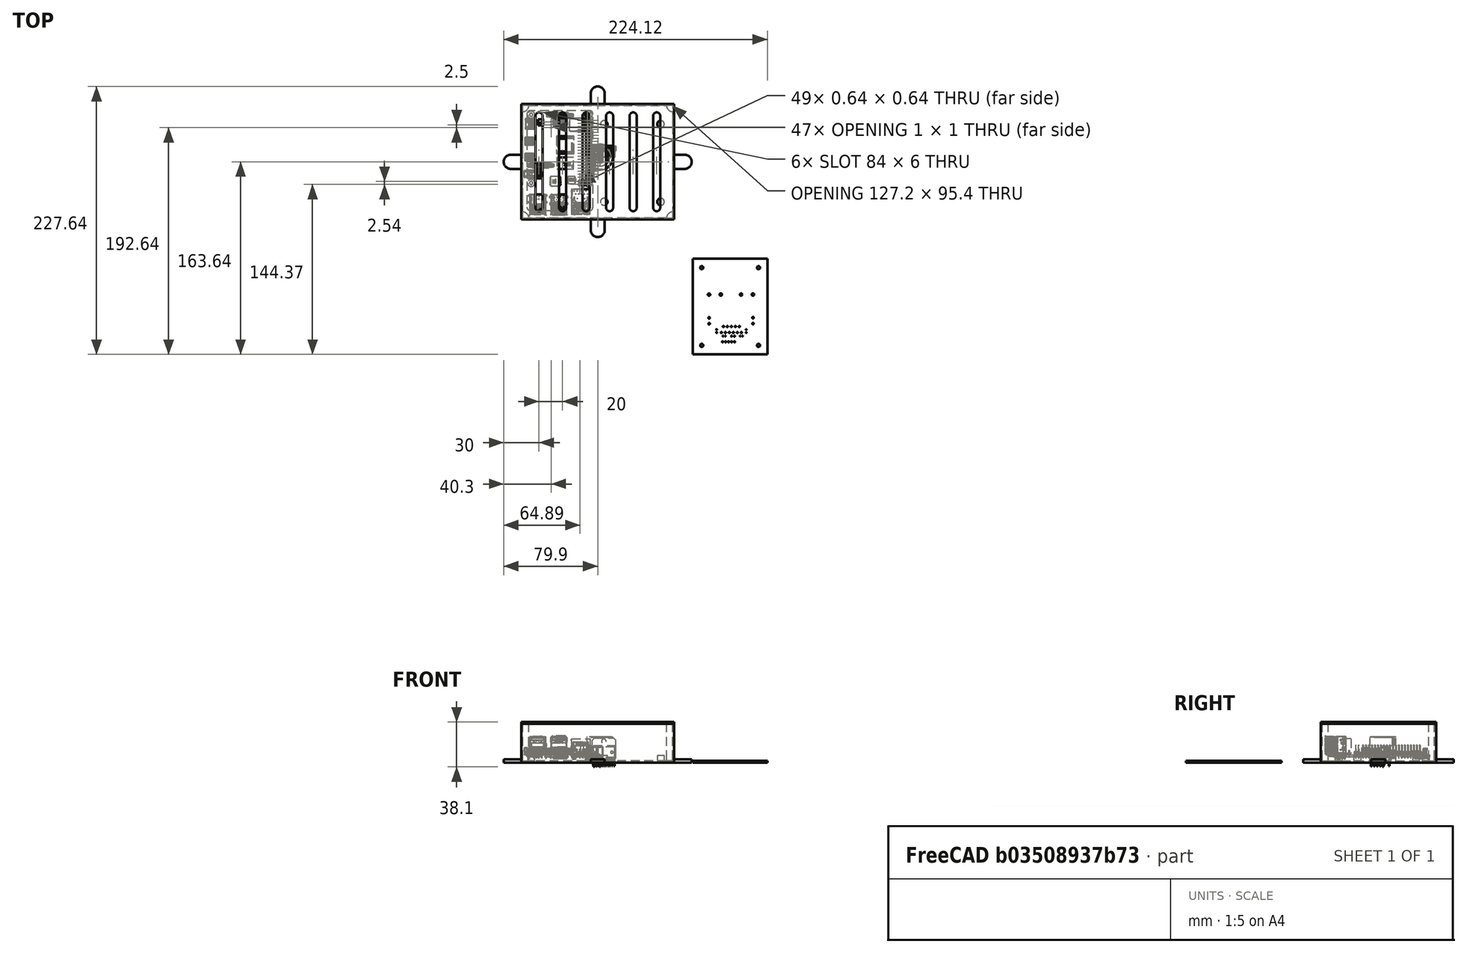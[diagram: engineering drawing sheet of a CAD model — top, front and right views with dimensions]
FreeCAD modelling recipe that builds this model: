
FCSTD DOCUMENT  (FreeCAD 0.19R)
Label: cmd-module-box
License: All rights reserved
LicenseURL: http://en.wikipedia.org/wiki/All_rights_reserved
objects: App::Part×14, Part::Feature×13, Sketcher::SketchObject×12, PartDesign::Pad×12, PartDesign::Body×12, Part::MultiFuse×6, Part::Fuse×4, Mesh::Feature×2
note: 71 computed .brp shape members not serialized (recipe doc carries the construction recipe); baked Part::Feature solids carry a one-line shape summary decoded from their .brp

FEATURE [Part::Feature] Feature  label="Raspberry Pi 4 Model B001"
  Placement = pos=(-29,-3,6) rot=(0.57735,-0.57735,-0.57735;2.0944rad)
  shape: bbox 58.41 x 89 x 19.91 mm, 10487 faces, 109 solids (baked)
FEATURE [Part::Feature] Part__Feature  label="SOLID"
  shape: bbox 2.54 x 12.7 x 11.54 mm, 124 faces (baked)
FEATURE [App::Part] PinHeader_1x05_P2_54mm_Vertical  label="PinHeader_1x05_P2.54mm_Vertical"
  Group = -> [Part__Feature]
  Origin = -> Origin012
  Placement = pos=(109.22,-156.972,1.65) rot=(0,0,1;1.5708rad)
FEATURE [Part::Feature] Part__Feature001  label="SOLID001"
  shape: bbox 10.74 x 9.8 x 17.3 mm, 89 faces (baked)
FEATURE [App::Part] TerminalBlock_Phoenix_MKDS_1_5_2_1x02_P5_00mm_Horizontal  label="TerminalBlock_Phoenix_MKDS-1,5-2_1x02_P5.00mm_Horizontal"
  Group = -> [Part__Feature001]
  Origin = -> Origin013
  Placement = pos=(135.128,-141.478,1.65) rot=(0,0,1;1.5708rad)
FEATURE [Part::Feature] Part__Feature002  label="SOLID002"
  shape: bbox 27.19 x 28.12 x 24 mm, 51 faces (baked)
FEATURE [App::Part] CP_Radial_D22_0mm_P10_00mm_SnapIn  label="CP_Radial_D22.0mm_P10.00mm_SnapIn"
  Group = -> [Part__Feature002]
  Origin = -> Origin002
  Placement = pos=(107.696,-116.84,1.65) rot=(0,0,1;3.14159rad)
FEATURE [Part::Feature] Part__Feature003  label="SOLID003"
  shape: bbox 27.19 x 28.12 x 24 mm, 51 faces (baked)
FEATURE [App::Part] CP_Radial_D22_0mm_P10_00mm_SnapIn001  label="CP_Radial_D22.0mm_P10.00mm_SnapIn001"
  Group = -> [Part__Feature003]
  Origin = -> Origin003
  Placement = pos=(124.968,-116.84,1.65) rot=(0,0,1;0rad)
FEATURE [Part::Feature] Part__Feature004  label="SOLID004"
  shape: bbox 20 x 9.88 x 24 mm, 166 faces (baked)
FEATURE [App::Part] TO_220_11_P3_4x5_08mm_StaggerOdd_Lead4_85mm_Vertical  label="TO-220-11_P3.4x5.08mm_StaggerOdd_Lead4.85mm_Vertical"
  Group = -> [Part__Feature004]
  Origin = -> Origin004
  Placement = pos=(108.204,-149.098,1.65) rot=(0,0,1;0rad)
FEATURE [Part::Feature] Part__Feature005  label="SOLID005"
  shape: bbox 3.098 x 1.732 x 9.682 mm, 17 faces (baked)
FEATURE [App::Part] R_Axial_DIN0204_L3_6mm_D1_6mm_P1_90mm_Vertical  label="R_Axial_DIN0204_L3.6mm_D1.6mm_P1.90mm_Vertical"
  Group = -> [Part__Feature005]
  Origin = -> Origin005
  Placement = pos=(111.506,-152.146,1.65) rot=(0,0,1;3.14159rad)
FEATURE [Part::Feature] Part__Feature006  label="SOLID006"
  shape: bbox 3.098 x 1.732 x 9.682 mm, 17 faces (baked)
FEATURE [App::Part] R_Axial_DIN0204_L3_6mm_D1_6mm_P1_90mm_Vertical001  label="R_Axial_DIN0204_L3.6mm_D1.6mm_P1.90mm_Vertical001"
  Group = -> [Part__Feature006]
  Origin = -> Origin006
  Placement = pos=(124.206,-152.146,1.65) rot=(0,0,1;0rad)
FEATURE [Part::Feature] Part__Feature007  label="SOLID007"
  shape: bbox 10.74 x 9.8 x 17.3 mm, 89 faces (baked)
FEATURE [App::Part] TerminalBlock_Phoenix_MKDS_1_5_2_1x02_P5_00mm_Horizontal001  label="TerminalBlock_Phoenix_MKDS-1,5-2_1x02_P5.00mm_Horizontal001"
  Group = -> [Part__Feature007]
  Origin = -> Origin007
  Placement = pos=(97.79,-136.652,1.65) rot=(0,0,-1;1.5708rad)
FEATURE [Part::Feature] Part__Feature008  label="SOLID008"
  shape: bbox 3 x 1.6 x 5.1 mm, 12 faces (baked)
FEATURE [App::Part] C_Disc_D3_0mm_W1_6mm_P2_50mm  label="C_Disc_D3.0mm_W1.6mm_P2.50mm"
  Group = -> [Part__Feature008]
  Origin = -> Origin008
  Placement = pos=(129.286,-149.098,1.65) rot=(0,0,1;1.5708rad)
FEATURE [Part::Feature] Part__Feature009  label="SOLID009"
  shape: bbox 3 x 1.6 x 5.1 mm, 12 faces (baked)
FEATURE [App::Part] C_Disc_D3_0mm_W1_6mm_P2_50mm001  label="C_Disc_D3.0mm_W1.6mm_P2.50mm001"
  Group = -> [Part__Feature009]
  Origin = -> Origin009
  Placement = pos=(104.14,-146.558,1.65) rot=(0,0,-1;1.5708rad)
FEATURE [Part::Feature] Part__Feature010  label="SOLID010"
  shape: bbox 3 x 1.6 x 5.1 mm, 12 faces (baked)
FEATURE [App::Part] C_Disc_D3_0mm_W1_6mm_P2_50mm002  label="C_Disc_D3.0mm_W1.6mm_P2.50mm002"
  Group = -> [Part__Feature010]
  Origin = -> Origin010
  Placement = pos=(116.84,-152.146,1.65) rot=(0,0,1;0rad)
FEATURE [Part::Feature] Part__Feature011  label="COMPOUND"
  shape: bbox 63.5 x 81.28 x 1.6 mm, 44 faces (baked)
FEATURE [App::Part] Open_CASCADE_STEP_translator_6_9_1  label="Open CASCADE STEP translator 6.9 1"
  Group = -> [PinHeader_1x05_P2_54mm_Vertical,TerminalBlock_Phoenix_MKDS_1_5_2_1x02_P5_00mm_Horizontal,CP_Radial_D22_0mm_P10_00mm_SnapIn,CP_Radial_D22_0mm_P10_00mm_SnapIn001,TO_220_11_P3_4x5_08mm_StaggerOdd_Lead4_85mm_Vertical,R_Axial_DIN0204_L3_6mm_D1_6mm_P1_90mm_Vertical,R_Axial_DIN0204_L3_6mm_D1_6mm_P1_90mm_Vertical001,TerminalBlock_Phoenix_MKDS_1_5_2_1x02_P5_00mm_Horizontal001,C_Disc_D3_0mm_W1_6mm_P2_50mm,+3 more]
  Origin = -> Origin011
  Placement = pos=(-83,122,5) rot=(0,0,1;0rad)
FEATURE [Sketcher::SketchObject] Sketch
  FullyConstrained = true
  MapMode = 5
  Support = -> [XY_Plane014]
  sketch-geometry (28):
    g0: LineSegment StartX=-55.5 StartY=43.7 StartZ=0 EndX=61.7 EndY=43.7 EndZ=0
    g1: LineSegment StartX=66.7 StartY=38.7 StartZ=0 EndX=66.7 EndY=-46.7 EndZ=0
    g2: LineSegment StartX=61.7 StartY=-51.7 StartZ=0 EndX=-55.5 EndY=-51.7 EndZ=0
    g3: LineSegment StartX=-60.5 StartY=-46.7 StartZ=0 EndX=-60.5 EndY=38.7 EndZ=0
    g4: LineSegment StartX=-61.8 StartY=45 StartZ=0 EndX=-2.9 EndY=45 EndZ=0
    g5: LineSegment StartX=68 StartY=45 StartZ=0 EndX=68 EndY=2 EndZ=0
    g6: LineSegment StartX=68 StartY=-53 StartZ=0 EndX=9.1 EndY=-53 EndZ=0
    g7: LineSegment StartX=-61.8 StartY=-53 StartZ=0 EndX=-61.8 EndY=-10 EndZ=0
    g8: ArcOfCircle CenterX=-70.8 CenterY=-4 CenterZ=0 NormalX=0 NormalY=0 NormalZ=1 AngleXU=0 Radius=6 StartAngle=1.5708 EndAngle=4.71239
    g9: LineSegment StartX=-61.8 StartY=2 StartZ=0 EndX=-70.8 EndY=2 EndZ=0
    g10: LineSegment StartX=-61.8 StartY=-10 StartZ=0 EndX=-70.8 EndY=-10 EndZ=0
    g11: LineSegment StartX=-61.8 StartY=2 StartZ=0 EndX=-61.8 EndY=45 EndZ=0
    g12: ArcOfCircle CenterX=-60.5 CenterY=-51.7 CenterZ=0 NormalX=0 NormalY=0 NormalZ=1 AngleXU=0 Radius=5 StartAngle=5e-16 EndAngle=1.5708
    g13: ArcOfCircle CenterX=-60.5 CenterY=43.7 CenterZ=0 NormalX=0 NormalY=0 NormalZ=1 AngleXU=0 Radius=5 StartAngle=4.71239 EndAngle=6.28319
    g14: ArcOfCircle CenterX=66.7 CenterY=43.7 CenterZ=0 NormalX=0 NormalY=0 NormalZ=1 AngleXU=0 Radius=5 StartAngle=3.14159 EndAngle=4.71239
    g15: ArcOfCircle CenterX=66.7 CenterY=-51.7 CenterZ=0 NormalX=0 NormalY=0 NormalZ=1 AngleXU=0 Radius=5 StartAngle=1.5708 EndAngle=3.14159
    g16: ArcOfCircle CenterX=3.1 CenterY=54 CenterZ=0 NormalX=0 NormalY=0 NormalZ=1 AngleXU=0 Radius=6 StartAngle=-2.49e-14 EndAngle=3.14159
    g17: LineSegment StartX=-2.9 StartY=54 StartZ=0 EndX=-2.9 EndY=45 EndZ=0
    g18: LineSegment StartX=9.1 StartY=54 StartZ=0 EndX=9.1 EndY=45 EndZ=0
    g19: LineSegment StartX=9.1 StartY=45 StartZ=0 EndX=68 EndY=45 EndZ=0
    g20: ArcOfCircle CenterX=77 CenterY=-4 CenterZ=0 NormalX=0 NormalY=0 NormalZ=1 AngleXU=0 Radius=6 StartAngle=4.71239 EndAngle=7.85398
    g21: LineSegment StartX=77 StartY=2 StartZ=0 EndX=68 EndY=2 EndZ=0
    g22: LineSegment StartX=77 StartY=-10 StartZ=0 EndX=68 EndY=-10 EndZ=0
    g23: LineSegment StartX=68 StartY=-10 StartZ=0 EndX=68 EndY=-53 EndZ=0
    g24: ArcOfCircle CenterX=3.1 CenterY=-62 CenterZ=0 NormalX=0 NormalY=0 NormalZ=1 AngleXU=0 Radius=6 StartAngle=3.14159 EndAngle=6.28319
    g25: LineSegment StartX=9.1 StartY=-62 StartZ=0 EndX=9.1 EndY=-53 EndZ=0
    g26: LineSegment StartX=-2.9 StartY=-62 StartZ=0 EndX=-2.9 EndY=-53 EndZ=0
    g27: LineSegment StartX=-2.9 StartY=-53 StartZ=0 EndX=-61.8 EndY=-53 EndZ=0
  constraints (80):
    c: Horizontal(g0)
    c: Horizontal(g2)
    c: Vertical(g1)
    c: Vertical(g3)
    c: Coincident(g19,g5)
    c: Coincident(g23,g6)
    c: Coincident(g27,g7)
    c: Coincident(g11,g4)
    c: Horizontal(g4)
    c: Horizontal(g6)
    c: Vertical(g5)
    c: Vertical(g7)
    c: Distance(g12,g6) = 1.3
    c: Distance(g12,g7) = 1.3
    c: Distance(g15,g5) = 1.3
    c: Distance(g14,g4) = 1.3
    c: Tangent(g9,g8) = -1.5708
    c: Tangent(g10,g8) = 1.5708
    c: Horizontal(g9)
    c: Radius(g8) = 6
    c: Tangent(g7,g11)
    c: Horizontal(g10)
    c: DistanceY(g-1,g23) = -53
    c: DistanceX(g-2,g19) = 68
    c: Radius(g12) = 5
    c: Coincident(g2,g12)
    c: Coincident(g3,g12)
    c: Radius(g13) = 5
    c: Coincident(g3,g13)
    c: Coincident(g0,g13)
    c: Radius(g14) = 5
    c: Coincident(g1,g14)
    c: Coincident(g0,g14)
    c: Radius(g15) = 5
    c: Coincident(g2,g15)
    c: Coincident(g1,g15)
    c: DistanceX(g-2,g4) = -61.8
    c: Coincident(g9,g11)
    c: Coincident(g10,g7)
    c: Distance(g13,g4) = 1.3
    c: Distance(g13,g11) = 1.3
    c: Distance(g0,g4) = 1.3
    c: Distance(g3,g11) = 1.3
    c: Distance(g1,g5) = 1.3
    c: Distance(g2,g6) = 1.3
    c: Distance(g8,g4) = 49
    c: Distance(g14,g5) = 1.3
    c: Distance(g15,g6) = 1.3
    c: Distance(g9) = 9
    c: Tangent(g16,g18) = 1.5708
    c: Tangent(g16,g17) = -1.5708
    c: Vertical(g17)
    c: Distance(g16,g11) = 64.9
    c: Radius(g16) = 6
    c: Coincident(g4,g17)
    c: Coincident(g19,g18)
    c: Tangent(g4,g19)
    c: Vertical(g18)
    c: Distance(g18) = 9
    c: Tangent(g20,g22) = 1.5708
    c: Tangent(g20,g21) = -1.5708
    c: Horizontal(g21)
    c: Horizontal(g22)
    c: Coincident(g5,g21)
    c: Coincident(g23,g22)
    c: Tangent(g5,g23)
    c: Distance(g6,g19) = 98
    c: Radius(g20) = 6
    c: Distance(g21) = 9
    c: Distance(g20,g19) = 49
    c: Tangent(g24,g26) = 1.5708
    c: Tangent(g24,g25) = -1.5708
    c: Vertical(g25)
    c: Vertical(g26)
    c: Radius(g24) = 6
    c: Coincident(g6,g25)
    c: Coincident(g27,g26)
    c: Tangent(g6,g27)
    c: Distance(g24,g7) = 64.9
    c: Distance(g25) = 9
FEATURE [Sketcher::SketchObject] Sketch001
  FullyConstrained = true
  MapMode = 5
  Support = -> [XY_Plane015]
  sketch-geometry (8):
    g0: LineSegment StartX=-55.5 StartY=43.7 StartZ=0 EndX=61.7 EndY=43.7 EndZ=0
    g1: LineSegment StartX=66.7 StartY=38.7 StartZ=0 EndX=66.7 EndY=-46.7 EndZ=0
    g2: LineSegment StartX=61.7 StartY=-51.7 StartZ=0 EndX=-55.5 EndY=-51.7 EndZ=0
    g3: LineSegment StartX=-60.5 StartY=-46.7 StartZ=0 EndX=-60.5 EndY=38.7 EndZ=0
    g4: ArcOfCircle CenterX=-60.5 CenterY=-51.7 CenterZ=0 NormalX=0 NormalY=0 NormalZ=1 AngleXU=0 Radius=5 StartAngle=5e-16 EndAngle=1.5708
    g5: ArcOfCircle CenterX=-60.5 CenterY=43.7 CenterZ=0 NormalX=0 NormalY=0 NormalZ=1 AngleXU=0 Radius=5 StartAngle=4.71239 EndAngle=6.28319
    g6: ArcOfCircle CenterX=66.7 CenterY=43.7 CenterZ=0 NormalX=0 NormalY=0 NormalZ=1 AngleXU=0 Radius=5 StartAngle=3.14159 EndAngle=4.71239
    g7: ArcOfCircle CenterX=66.7 CenterY=-51.7 CenterZ=0 NormalX=0 NormalY=0 NormalZ=1 AngleXU=0 Radius=5 StartAngle=1.5708 EndAngle=3.14159
  constraints (28):
    c: Horizontal(g0)
    c: Horizontal(g2)
    c: Vertical(g1)
    c: Vertical(g3)
    c: Radius(g4) = 5
    c: Coincident(g2,g4)
    c: Coincident(g3,g4)
    c: Radius(g5) = 5
    c: Coincident(g3,g5)
    c: Coincident(g0,g5)
    c: Radius(g6) = 5
    c: Coincident(g1,g6)
    c: Coincident(g0,g6)
    c: Radius(g7) = 5
    c: Coincident(g2,g7)
    c: Coincident(g1,g7)
    c: DistanceY(g-1,g6) = 43.7
    c: DistanceY(g-1,g7) = -51.7
    c: DistanceY(g-1,g4) = -51.7
    c: DistanceY(g-1,g5) = 43.7
    c: Distance(g0) = 117.2
    c: DistanceX(g-2,g3) = -60.5
    c: DistanceY(g-1,g2) = -51.7
    c: DistanceX(g-2,g1) = 66.7
    c: DistanceX(g-2,g6) = 66.7
    c: DistanceX(g-2,g7) = 66.7
    c: DistanceX(g-2,g4) = -60.5
    c: DistanceY(g-1,g0) = 43.7
FEATURE [PartDesign::Pad] Pad
  Direction = (1,1,1)
  Length = 3
  Length2 = 100
  Profile = -> Sketch
  Type = 0
FEATURE [PartDesign::Body] Body
  Group = -> [Sketch,Pad]
  Origin = -> Origin014
  Tip = -> Pad
FEATURE [Sketcher::SketchObject] Sketch002
  FullyConstrained = true
  MapMode = 5
  Support = -> [XY_Plane016]
  sketch-geometry (12):
    g0: LineSegment StartX=-55.5 StartY=43.7 StartZ=0 EndX=61.7 EndY=43.7 EndZ=0
    g1: LineSegment StartX=66.7 StartY=38.7 StartZ=0 EndX=66.7 EndY=-46.7 EndZ=0
    g2: LineSegment StartX=61.7 StartY=-51.7 StartZ=0 EndX=-55.5 EndY=-51.7 EndZ=0
    g3: LineSegment StartX=-60.5 StartY=-46.7 StartZ=0 EndX=-60.5 EndY=38.7 EndZ=0
    g4: LineSegment StartX=68 StartY=45 StartZ=0 EndX=68 EndY=-53 EndZ=0
    g5: LineSegment StartX=68 StartY=-53 StartZ=0 EndX=-61.8 EndY=-53 EndZ=0
    g6: LineSegment StartX=-61.8 StartY=-53 StartZ=0 EndX=-61.8 EndY=45 EndZ=0
    g7: ArcOfCircle CenterX=-60.5 CenterY=-51.7 CenterZ=0 NormalX=0 NormalY=0 NormalZ=1 AngleXU=0 Radius=5 StartAngle=4e-16 EndAngle=1.5708
    g8: ArcOfCircle CenterX=-60.5 CenterY=43.7 CenterZ=0 NormalX=0 NormalY=0 NormalZ=1 AngleXU=0 Radius=5 StartAngle=4.71239 EndAngle=6.28319
    g9: ArcOfCircle CenterX=66.7 CenterY=43.7 CenterZ=0 NormalX=0 NormalY=0 NormalZ=1 AngleXU=0 Radius=5 StartAngle=3.14159 EndAngle=4.71239
    g10: ArcOfCircle CenterX=66.7 CenterY=-51.7 CenterZ=0 NormalX=0 NormalY=0 NormalZ=1 AngleXU=0 Radius=5 StartAngle=1.5708 EndAngle=3.14159
    g11: LineSegment StartX=-61.8 StartY=45 StartZ=0 EndX=68 EndY=45 EndZ=0
  constraints (43):
    c: Horizontal(g0)
    c: Horizontal(g2)
    c: Vertical(g1)
    c: Vertical(g3)
    c: Coincident(g11,g4)
    c: Horizontal(g5)
    c: Vertical(g4)
    c: Distance(g7,g5) = 1.3
    c: Distance(g10,g4) = 1.3
    c: DistanceY(g-1,g5) = -53
    c: DistanceX(g-2,g11) = 68
    c: Radius(g7) = 5
    c: Coincident(g2,g7)
    c: Coincident(g3,g7)
    c: Radius(g8) = 5
    c: Coincident(g3,g8)
    c: Coincident(g0,g8)
    c: Radius(g9) = 5
    c: Coincident(g1,g9)
    c: Coincident(g0,g9)
    c: Radius(g10) = 5
    c: Coincident(g2,g10)
    c: Coincident(g1,g10)
    c: DistanceX(g-2,g6) = -61.8
    c: Distance(g8,g6) = 1.3
    c: Distance(g3,g6) = 1.3
    c: Distance(g1,g4) = 1.3
    c: Distance(g2,g5) = 1.3
    c: Distance(g9,g4) = 1.3
    c: Distance(g10,g5) = 1.3
    c: Distance(g5,g11) = 98
    c: PointOnObject(g5,g6)
    c: PointOnObject(g4,g5)
    c: Distance(g2) = 117.2
    c: Distance(g3) = 85.4
    c: Distance(g6) = 98
    c: Distance(g0) = 117.2
    c: Horizontal(g11)
    c: PointOnObject(g11,g6)
    c: Distance(g1) = 85.4
    c: DistanceY(g-1,g6) = 45
    c: DistanceY(g-1,g0) = 43.7
    c: Distance(g5) = 129.8
FEATURE [PartDesign::Pad] Pad001
  Direction = (1,1,1)
  Length = 1.6
  Length2 = 100
  Profile = -> Sketch001
  Type = 0
FEATURE [PartDesign::Body] Body001
  Group = -> [Sketch001,Pad001]
  Origin = -> Origin015
  Tip = -> Pad001
FEATURE [Part::Fuse] Fusion
  Base = -> Body
  Tool = -> Body001
FEATURE [Sketcher::SketchObject] Sketch003
  FullyConstrained = true
  MapMode = 5
  Support = -> [XY_Plane017]
  sketch-geometry (28):
    g0: LineSegment StartX=-61.8 StartY=45 StartZ=0 EndX=68 EndY=45 EndZ=0
    g1: LineSegment StartX=68 StartY=45 StartZ=0 EndX=68 EndY=-53 EndZ=0
    g2: LineSegment StartX=-61.8 StartY=-53 StartZ=0 EndX=-61.8 EndY=45 EndZ=0
    g3: LineSegment StartX=-61.8 StartY=-53 StartZ=0 EndX=68 EndY=-53 EndZ=0
    g4: ArcOfCircle CenterX=-46.8 CenterY=35 CenterZ=0 NormalX=0 NormalY=0 NormalZ=1 AngleXU=0 Radius=3 StartAngle=-1.8e-15 EndAngle=3.14159
    g5: ArcOfCircle CenterX=-46.8 CenterY=-43 CenterZ=0 NormalX=0 NormalY=0 NormalZ=1 AngleXU=0 Radius=3 StartAngle=3.14159 EndAngle=6.28319
    g6: LineSegment StartX=-49.8 StartY=35 StartZ=0 EndX=-49.8 EndY=-43 EndZ=0
    g7: LineSegment StartX=-43.8 StartY=35 StartZ=0 EndX=-43.8 EndY=-43 EndZ=0
    g8: ArcOfCircle CenterX=-26.8 CenterY=35 CenterZ=0 NormalX=0 NormalY=0 NormalZ=1 AngleXU=0 Radius=3 StartAngle=5e-16 EndAngle=3.14159
    g9: ArcOfCircle CenterX=-26.8 CenterY=-43 CenterZ=0 NormalX=0 NormalY=0 NormalZ=1 AngleXU=0 Radius=3 StartAngle=3.14159 EndAngle=6.28319
    g10: LineSegment StartX=-29.8 StartY=35 StartZ=0 EndX=-29.8 EndY=-43 EndZ=0
    g11: LineSegment StartX=-23.8 StartY=35 StartZ=0 EndX=-23.8 EndY=-43 EndZ=0
    g12: ArcOfCircle CenterX=-6.8 CenterY=35 CenterZ=0 NormalX=0 NormalY=0 NormalZ=1 AngleXU=0 Radius=3 StartAngle=7e-16 EndAngle=3.14159
    g13: ArcOfCircle CenterX=-6.8 CenterY=-43 CenterZ=0 NormalX=0 NormalY=0 NormalZ=1 AngleXU=0 Radius=3 StartAngle=3.14159 EndAngle=6.28319
    g14: LineSegment StartX=-9.8 StartY=35 StartZ=0 EndX=-9.8 EndY=-43 EndZ=0
    g15: LineSegment StartX=-3.8 StartY=35 StartZ=0 EndX=-3.8 EndY=-43 EndZ=0
    g16: ArcOfCircle CenterX=13.2 CenterY=35 CenterZ=0 NormalX=0 NormalY=0 NormalZ=1 AngleXU=0 Radius=3 StartAngle=-9e-16 EndAngle=3.14159
    g17: ArcOfCircle CenterX=13.2 CenterY=-43 CenterZ=0 NormalX=0 NormalY=0 NormalZ=1 AngleXU=0 Radius=3 StartAngle=3.14159 EndAngle=6.28319
    g18: LineSegment StartX=10.2 StartY=35 StartZ=0 EndX=10.2 EndY=-43 EndZ=0
    g19: LineSegment StartX=16.2 StartY=35 StartZ=0 EndX=16.2 EndY=-43 EndZ=0
    g20: ArcOfCircle CenterX=33.2 CenterY=35 CenterZ=0 NormalX=0 NormalY=0 NormalZ=1 AngleXU=0 Radius=3 StartAngle=-9e-16 EndAngle=3.14159
    g21: ArcOfCircle CenterX=33.2 CenterY=-43 CenterZ=0 NormalX=0 NormalY=0 NormalZ=1 AngleXU=0 Radius=3 StartAngle=3.14159 EndAngle=6.28319
    g22: LineSegment StartX=30.2 StartY=35 StartZ=0 EndX=30.2 EndY=-43 EndZ=0
    g23: LineSegment StartX=36.2 StartY=35 StartZ=0 EndX=36.2 EndY=-43 EndZ=0
    g24: ArcOfCircle CenterX=53.2 CenterY=35 CenterZ=0 NormalX=0 NormalY=0 NormalZ=1 AngleXU=0 Radius=3 StartAngle=-9e-16 EndAngle=3.14159
    g25: ArcOfCircle CenterX=53.2 CenterY=-43 CenterZ=0 NormalX=0 NormalY=0 NormalZ=1 AngleXU=0 Radius=3 StartAngle=3.14159 EndAngle=6.28319
    g26: LineSegment StartX=50.2 StartY=35 StartZ=0 EndX=50.2 EndY=-43 EndZ=0
    g27: LineSegment StartX=56.2 StartY=35 StartZ=0 EndX=56.2 EndY=-43 EndZ=0
  constraints (73):
    c: Coincident(g2,g0)
    c: Horizontal(g0)
    c: Vertical(g1)
    c: DistanceX(g-2,g1) = 68
    c: DistanceX(g-2,g0) = -61.8
    c: Vertical(g2)
    c: Distance(g2) = 98
    c: DistanceY(g-1,g1) = 45
    c: DistanceY(g-1,g0) = 45
    c: PointOnObject(g0,g1)
    c: Coincident(g3,g2)
    c: Coincident(g3,g1)
    c: Horizontal(g3)
    c: Tangent(g4,g7) = 1.5708
    c: Tangent(g4,g6) = -1.5708
    c: Tangent(g6,g5) = -1.5708
    c: Tangent(g7,g5) = 1.5708
    c: Vertical(g6)
    c: Equal(g4,g5)
    c: Distance(g4,g0) = 10
    c: Distance(g5,g3) = 10
    c: Radius(g4) = 3
    c: Distance(g4,g2) = 15
    c: Tangent(g8,g11) = 1.5708
    c: Tangent(g8,g10) = -1.5708
    c: Tangent(g10,g9) = -1.5708
    c: Tangent(g11,g9) = 1.5708
    c: Vertical(g10)
    c: Equal(g8,g9)
    c: Equal(g4,g8) = 3
    c: Distance(g8,g4) = 20
    c: Tangent(g12,g15) = 1.5708
    c: Tangent(g12,g14) = -1.5708
    c: Tangent(g14,g13) = -1.5708
    c: Tangent(g15,g13) = 1.5708
    c: Vertical(g14)
    c: Equal(g12,g13)
    c: Distance(g12,g8) = 20
    c: Radius(g12) = 3
    c: Tangent(g16,g19) = 1.5708
    c: Tangent(g16,g18) = -1.5708
    c: Tangent(g18,g17) = -1.5708
    c: Tangent(g19,g17) = 1.5708
    c: Vertical(g18)
    c: Equal(g16,g17)
    c: Equal(g12,g16) = 3
    c: Distance(g16,g12) = 20
    c: Tangent(g20,g23) = 1.5708
    c: Tangent(g20,g22) = -1.5708
    c: Tangent(g22,g21) = -1.5708
    c: Tangent(g23,g21) = 1.5708
    c: Vertical(g22)
    c: Equal(g20,g21)
    c: Distance(g20,g16) = 20
    c: Distance(g21,g3) = 10
    c: Distance(g20,g0) = 10
    c: Distance(g16,g0) = 10
    c: Distance(g17,g3) = 10
    c: Distance(g13,g3) = 10
    c: Distance(g12,g0) = 10
    c: Distance(g9,g3) = 10
    c: Distance(g8,g0) = 10
    c: Radius(g20) = 3
    c: Tangent(g24,g27) = 1.5708
    c: Tangent(g24,g26) = -1.5708
    c: Tangent(g26,g25) = -1.5708
    c: Tangent(g27,g25) = 1.5708
    c: Vertical(g26)
    c: Equal(g24,g25)
    c: Equal(g20,g24) = 3
    c: Distance(g24,g20) = 20
    c: Distance(g24,g0) = 10
    c: Distance(g25,g3) = 10
FEATURE [PartDesign::Pad] Pad002
  Direction = (1,1,1)
  Length = 33
  Length2 = 100
  Profile = -> Sketch002
  Type = 0
FEATURE [PartDesign::Body] Body002
  Group = -> [Sketch002,Pad002]
  Origin = -> Origin016
  Tip = -> Pad002
FEATURE [Part::Fuse] Fusion001
  Base = -> Body002
  Tool = -> Fusion
FEATURE [PartDesign::Pad] Pad003
  Direction = (1,1,1)
  Length = 1.6
  Length2 = 100
  Profile = -> Sketch003
  Type = 0
FEATURE [PartDesign::Body] Body003
  Group = -> [Sketch003,Pad003]
  Origin = -> Origin017
  Placement = pos=(0,0,33) rot=(0,0,1;0rad)
  Tip = -> Pad003
FEATURE [Sketcher::SketchObject] Sketch004
  FullyConstrained = true
  MapMode = 5
  Support = -> [XY_Plane018]
  sketch-geometry (1):
    g0: Circle CenterX=-53.5 CenterY=36 CenterZ=0 NormalX=0 NormalY=0 NormalZ=1 AngleXU=0 Radius=3
  constraints (3):
    c: Radius(g0) = 3
    c: DistanceY(g-1,g0) = 36
    c: DistanceX(g-2,g0) = -53.5
FEATURE [Sketcher::SketchObject] Sketch005
  FullyConstrained = true
  MapMode = 5
  Support = -> [XY_Plane019]
  sketch-geometry (1):
    g0: Circle CenterX=-4.5 CenterY=36 CenterZ=0 NormalX=0 NormalY=0 NormalZ=1 AngleXU=0 Radius=3
  constraints (3):
    c: Radius(g0) = 3
    c: DistanceX(g-2,g0) = -4.5
    c: DistanceY(g-1,g0) = 36
FEATURE [Sketcher::SketchObject] Sketch006
  FullyConstrained = true
  MapMode = 5
  Support = -> [XY_Plane020]
  sketch-geometry (1):
    g0: Circle CenterX=-4.5 CenterY=-22 CenterZ=0 NormalX=0 NormalY=0 NormalZ=1 AngleXU=0 Radius=3
  constraints (3):
    c: Radius(g0) = 3
    c: DistanceX(g-2,g0) = -4.5
    c: DistanceY(g-1,g0) = -22
FEATURE [Sketcher::SketchObject] Sketch007
  FullyConstrained = true
  MapMode = 5
  Support = -> [XY_Plane021]
  sketch-geometry (1):
    g0: Circle CenterX=-53.5 CenterY=-22 CenterZ=0 NormalX=0 NormalY=0 NormalZ=1 AngleXU=0 Radius=3
  constraints (3):
    c: Radius(g0) = 3
    c: DistanceY(g-1,g0) = -22
    c: DistanceX(g-2,g0) = -53.5
FEATURE [Sketcher::SketchObject] Sketch008
  FullyConstrained = true
  MapMode = 5
  Support = -> [XY_Plane022]
  sketch-geometry (1):
    g0: Circle CenterX=8.45 CenterY=28 CenterZ=0 NormalX=0 NormalY=0 NormalZ=1 AngleXU=0 Radius=3
  constraints (3):
    c: Radius(g0) = 3
    c: Distance(g0,g-2) = 8.45
    c: DistanceY(g-1,g0) = 28
FEATURE [Sketcher::SketchObject] Sketch009
  FullyConstrained = true
  MapMode = 5
  Support = -> [XY_Plane023]
  sketch-geometry (1):
    g0: Circle CenterX=56.65 CenterY=28 CenterZ=0 NormalX=0 NormalY=0 NormalZ=1 AngleXU=0 Radius=3
  constraints (3):
    c: Radius(g0) = 3
    c: DistanceY(g-1,g0) = 28
    c: DistanceX(g-2,g0) = 56.65
FEATURE [Sketcher::SketchObject] Sketch010
  FullyConstrained = true
  MapMode = 5
  Support = -> [XY_Plane024]
  sketch-geometry (1):
    g0: Circle CenterX=56.65 CenterY=-38 CenterZ=0 NormalX=0 NormalY=0 NormalZ=1 AngleXU=0 Radius=3
  constraints (3):
    c: Radius(g0) = 3
    c: DistanceY(g-1,g0) = -38
    c: DistanceX(g-2,g0) = 56.65
FEATURE [Sketcher::SketchObject] Sketch011
  FullyConstrained = true
  MapMode = 5
  Support = -> [XY_Plane025]
  sketch-geometry (1):
    g0: Circle CenterX=8.45 CenterY=-38 CenterZ=0 NormalX=0 NormalY=0 NormalZ=1 AngleXU=0 Radius=3
  constraints (3):
    c: Radius(g0) = 3
    c: DistanceX(g-2,g0) = 8.45
    c: DistanceY(g-1,g0) = -38
FEATURE [PartDesign::Pad] Pad004
  Direction = (1,1,1)
  Length = 6
  Length2 = 100
  Profile = -> Sketch004
  Type = 0
FEATURE [PartDesign::Body] Body004
  Group = -> [Sketch004,Pad004]
  Origin = -> Origin018
  Tip = -> Pad004
FEATURE [PartDesign::Pad] Pad005
  Direction = (1,1,1)
  Length = 6
  Length2 = 100
  Profile = -> Sketch005
  Type = 0
FEATURE [PartDesign::Body] Body005
  Group = -> [Sketch005,Pad005]
  Origin = -> Origin019
  Tip = -> Pad005
FEATURE [PartDesign::Pad] Pad006
  Direction = (1,1,1)
  Length = 6
  Length2 = 100
  Profile = -> Sketch006
  Type = 0
FEATURE [PartDesign::Body] Body006
  Group = -> [Sketch006,Pad006]
  Origin = -> Origin020
  Tip = -> Pad006
FEATURE [PartDesign::Pad] Pad007
  Direction = (1,1,1)
  Length = 6
  Length2 = 100
  Profile = -> Sketch007
  Type = 0
FEATURE [PartDesign::Body] Body007
  Group = -> [Sketch007,Pad007]
  Origin = -> Origin021
  Tip = -> Pad007
FEATURE [PartDesign::Pad] Pad008
  Direction = (1,1,1)
  Length = 6
  Length2 = 100
  Profile = -> Sketch008
  Type = 0
FEATURE [PartDesign::Body] Body008
  Group = -> [Sketch008,Pad008]
  Origin = -> Origin022
  Tip = -> Pad008
FEATURE [PartDesign::Pad] Pad009
  Direction = (1,1,1)
  Length = 6
  Length2 = 100
  Profile = -> Sketch009
  Type = 0
FEATURE [PartDesign::Body] Body009
  Group = -> [Sketch009,Pad009]
  Origin = -> Origin023
  Tip = -> Pad009
FEATURE [PartDesign::Pad] Pad010
  Direction = (1,1,1)
  Length = 6
  Length2 = 100
  Profile = -> Sketch010
  Type = 0
FEATURE [PartDesign::Body] Body010
  Group = -> [Sketch010,Pad010]
  Origin = -> Origin024
  Tip = -> Pad010
FEATURE [PartDesign::Pad] Pad011
  Direction = (1,1,1)
  Length = 6
  Length2 = 100
  Profile = -> Sketch011
  Type = 0
FEATURE [PartDesign::Body] Body011
  Group = -> [Sketch011,Pad011]
  Origin = -> Origin025
  Tip = -> Pad011
FEATURE [Part::Fuse] Fusion002
  Base = -> Fusion001
  Tool = -> Body004
FEATURE [Part::Fuse] Fusion003
  Base = -> Body005
  Tool = -> Fusion002
FEATURE [Part::MultiFuse] Fusion004
  Shapes = -> [Body006,Fusion003]
FEATURE [Part::MultiFuse] Fusion005
  Shapes = -> [Body007,Fusion004]
FEATURE [Part::MultiFuse] Fusion006
  Shapes = -> [Fusion005,Body008]
FEATURE [Part::MultiFuse] Fusion007
  Shapes = -> [Body009,Fusion006]
FEATURE [Part::MultiFuse] Fusion008
  Shapes = -> [Body010,Fusion007]
FEATURE [Part::MultiFuse] Fusion009
  Shapes = -> [Body011,Fusion008]
FEATURE [Mesh::Feature] Mesh  label="Box_Meshed"
FEATURE [App::Part] Part  label="main"
  Group = -> [Body,Body001,Body002,Fusion,Fusion001,Body004,Body005,Body006,Body007,Body008,Body009,Body010,Body011,Fusion002,Fusion003,Fusion004,Fusion005,Fusion006,Fusion007,Fusion008,Fusion009,Mesh]
  Origin = -> Origin
FEATURE [Mesh::Feature] Mesh001  label="Cap_Meshed"
FEATURE [App::Part] Part001  label="cap"
  Group = -> [Body003,Mesh001]
  Origin = -> Origin001
